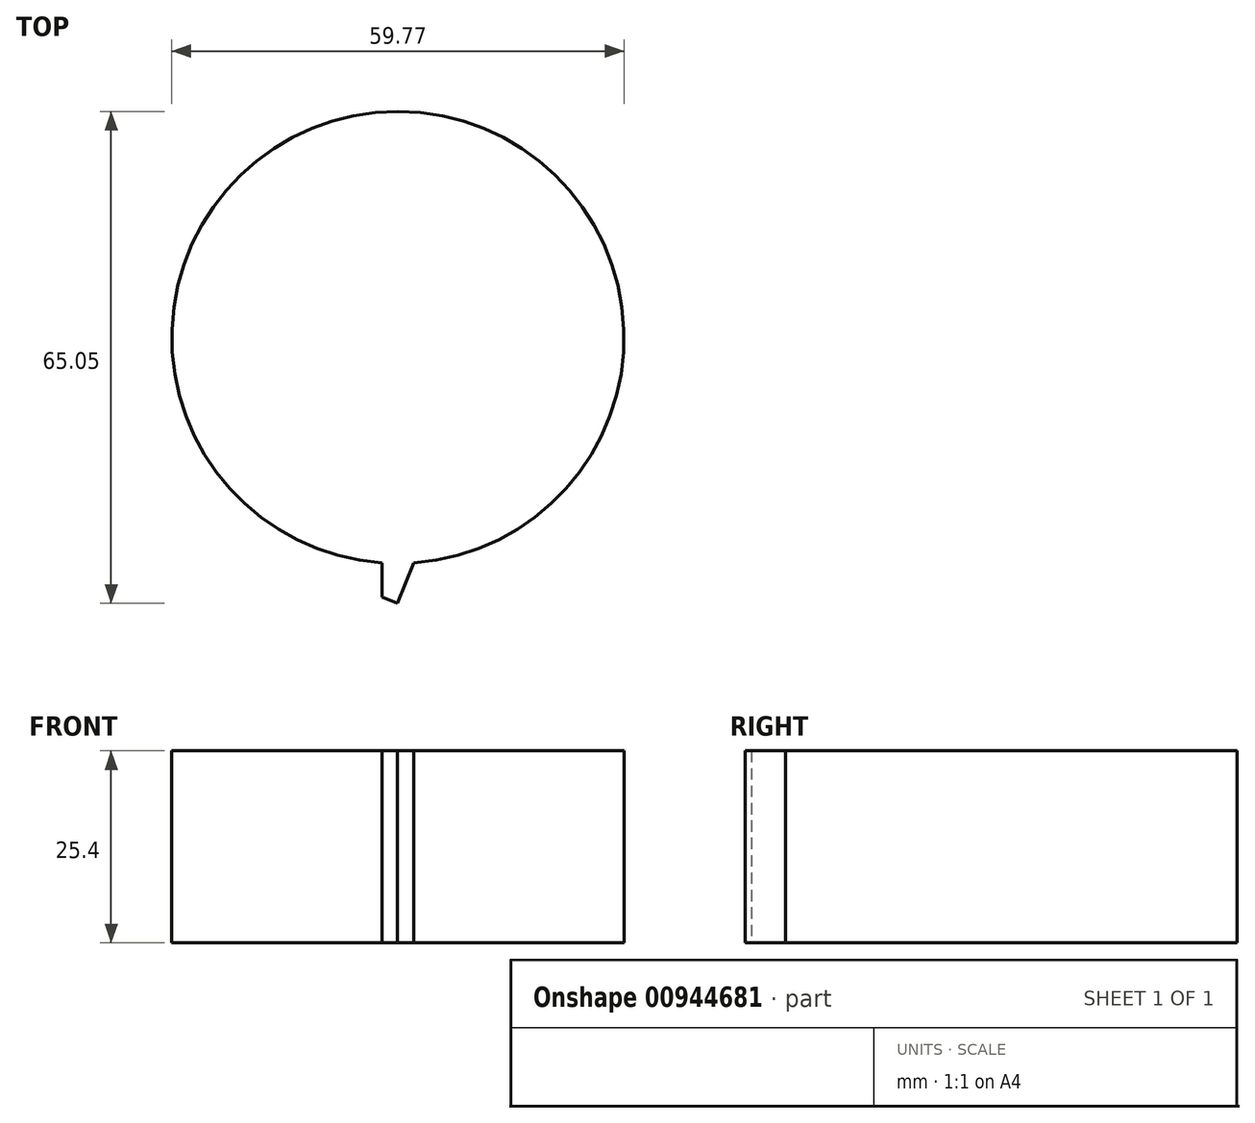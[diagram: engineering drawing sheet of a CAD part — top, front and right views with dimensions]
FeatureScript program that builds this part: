
annotation { "Feature Type Name" : "Feature", "Feature Type Description" : "" }
export const myFeature = defineFeature(function(context is Context, id is Id, definition is map)
    precondition{}
    {
        {
            var Q0;
            Q0=qCreatedBy(makeId("Top.planeOp"),FACE);
            var sketch = newSketch(context, id + "F0", { "sketchPlane" : qUnion([Q0])});
            skLineSegment(sketch, "E0", {"start": v(31.68, 0) * mm, "end": v(31.68, -4.53) * mm});
            skLineSegment(sketch, "E1", {"start": v(31.68, -4.53) * mm, "end": v(33.7, -5.36) * mm});
            skLineSegment(sketch, "E2", {"start": v(33.7, -5.36) * mm, "end": v(35.91, 0) * mm});
            skLineSegment(sketch, "E3", {"start": v(31.68, 0) * mm, "end": v(31.68, 0) * mm});
            skArc(sketch, "E4", {"start": v(35.91, 0) * mm, "mid": v(33.8, 59.7) * mm, "end": v(31.68, 0) * mm});
            skSolve(sketch);
        }
        {
            var Q0;
            Q0 = qSketchRegion(id + "F0", true);
            extrude(context, id + "F1", {"entities" : qUnion([Q0]), "depth" : 25.4 * mm, "offsetDistance" : 25.4 * mm});
        }
    });
